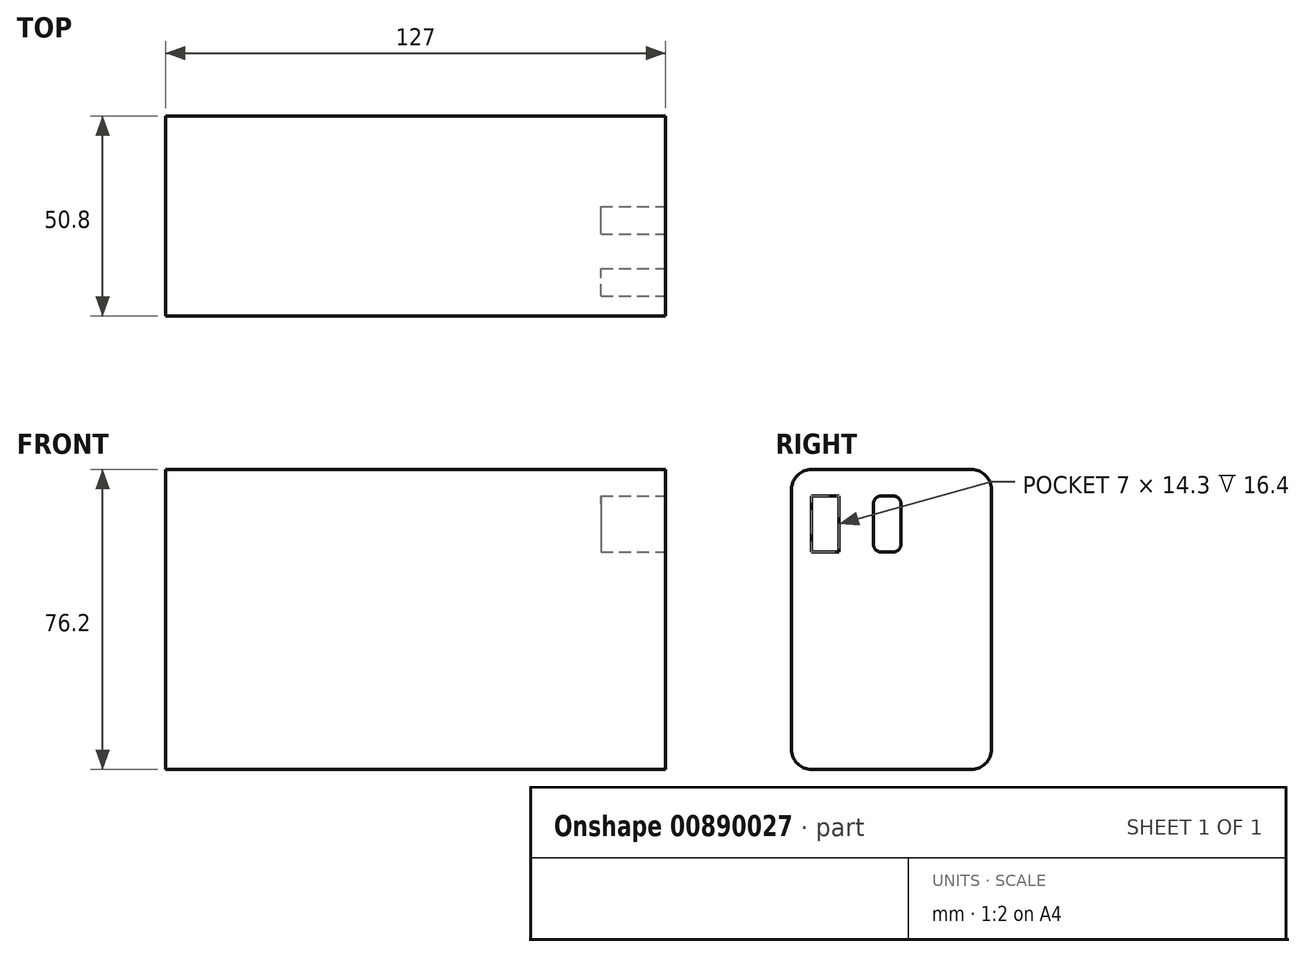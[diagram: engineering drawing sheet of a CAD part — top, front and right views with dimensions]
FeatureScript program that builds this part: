
annotation { "Feature Type Name" : "Feature", "Feature Type Description" : "" }
export const myFeature = defineFeature(function(context is Context, id is Id, definition is map)
    precondition{}
    {
        {
            var Q0;
            Q0=qCreatedBy(makeId("Front.planeOp"),FACE);
            var sketch = newSketch(context, id + "F0", { "sketchPlane" : qUnion([Q0])});
            skLineSegment(sketch, "E0.bottom", {"start": v(63.5, -38.1) * mm, "end": v(-63.5, -38.1) * mm});
            skLineSegment(sketch, "E0.top", {"start": v(63.5, 38.1) * mm, "end": v(-63.5, 38.1) * mm});
            skLineSegment(sketch, "E0.left", {"start": v(63.5, -38.1) * mm, "end": v(63.5, 38.1) * mm});
            skLineSegment(sketch, "E0.right", {"start": v(-63.5, -38.1) * mm, "end": v(-63.5, 38.1) * mm});
            skPoint(sketch, "E0.middle", {"position": v(0, 0) * mm});
            skSolve(sketch);
        }
        {
            var Q0;
            Q0=makeQuery(id+"F0.imprint","IMPRINT",FACE,{"disambiguationData":[TD([[makeQuery(id+"F0.imprint","IMPRINT",EDGE,{"derivedFrom":sQuery(id+"F0.wireOp",EDGE,"E0.bottom")}),-1.0]])]});
            extrude(context, id + "F1", {"entities" : qUnion([Q0]), "depth" : 50.8 * mm, "offsetDistance" : 25.4 * mm});
        }
        {
            var Q0;
            Q0=makeQuery(id+"F1.opExtrude","CAP_EDGE",EDGE,{"disambiguationData":[OSD([sQuery(id+"F0.wireOp",EDGE,"E0.top")])],"isStart":false});
            var Q1;
            Q1=makeQuery(id+"F1.opExtrude","CAP_EDGE",EDGE,{"disambiguationData":[OSD([sQuery(id+"F0.wireOp",EDGE,"E0.top")])],"isStart":true});
            var Q2;
            Q2=makeQuery(id+"F1.opExtrude","CAP_EDGE",EDGE,{"disambiguationData":[OSD([sQuery(id+"F0.wireOp",EDGE,"E0.bottom")])],"isStart":true});
            var Q3;
            Q3=makeQuery(id+"F1.opExtrude","CAP_EDGE",EDGE,{"disambiguationData":[OSD([sQuery(id+"F0.wireOp",EDGE,"E0.bottom")])],"isStart":false});
            fillet(context, id + "F2", {"entities" : qUnion([Q0, Q1, Q2, Q3]), "radius" : 5.08 * mm, "tangentPropagation" : true, "allowEdgeOverflow" : false});
        }
        {
            var Q0;
            Q0=makeQuery(id+"F1.opExtrude","SWEPT_FACE",FACE,{"disambiguationData":[OSD([sQuery(id+"F0.wireOp",EDGE,"E0.left")])]});
            var sketch = newSketch(context, id + "F3", { "sketchPlane" : qUnion([Q0])});
            skLineSegment(sketch, "E1.bottom", {"start": v(-45.72, 31.4) * mm, "end": v(-38.72, 31.4) * mm});
            skLineSegment(sketch, "E1.top", {"start": v(-45.72, 17.1) * mm, "end": v(-38.72, 17.1) * mm});
            skLineSegment(sketch, "E1.left", {"start": v(-45.72, 31.4) * mm, "end": v(-45.72, 17.1) * mm});
            skLineSegment(sketch, "E1.right", {"start": v(-38.72, 31.4) * mm, "end": v(-38.72, 17.1) * mm});
            skSolve(sketch);
        }
        {
            var Q0;
            Q0=makeQuery(id+"F3.imprint","IMPRINT",FACE,{"disambiguationData":[TD([[makeQuery(id+"F3.imprint","IMPRINT",EDGE,{"derivedFrom":sQuery(id+"F3.wireOp",EDGE,"E1.bottom")}),-1.0]])]});
            extrude(context, id + "F4", {"entities" : qUnion([Q0]), "operationType" : NewBodyOperationType.REMOVE, "oppositeDirection" : true, "depth" : 16.4 * mm, "offsetDistance" : 25.4 * mm});
        }
        {
            var Q0;
            Q0=makeQuery(id+"F1.opExtrude","SWEPT_FACE",FACE,{"disambiguationData":[OSD([sQuery(id+"F0.wireOp",EDGE,"E0.left")])]});
            var sketch = newSketch(context, id + "F5", { "sketchPlane" : qUnion([Q0])});
            skLineSegment(sketch, "E2.bottom", {"start": v(-27.99, 31.4) * mm, "end": v(-24.99, 31.4) * mm});
            skLineSegment(sketch, "E2.top", {"start": v(-27.99, 17.1) * mm, "end": v(-24.99, 17.1) * mm});
            skLineSegment(sketch, "E2.left", {"start": v(-29.99, 29.4) * mm, "end": v(-29.99, 19.1) * mm});
            skLineSegment(sketch, "E2.right", {"start": v(-22.99, 29.4) * mm, "end": v(-22.99, 19.1) * mm});
            skPoint(sketch, "E3.visualSharp", {"position": v(-29.99, 31.4) * mm});
            skArc(sketch, "E3.filletArc", {"start": v(-27.99, 31.4) * mm, "mid": v(-29.4, 30.81) * mm, "end": v(-29.99, 29.4) * mm});
            skPoint(sketch, "E4.visualSharp", {"position": v(-29.99, 17.1) * mm});
            skArc(sketch, "E4.filletArc", {"start": v(-29.99, 19.1) * mm, "mid": v(-29.4, 17.69) * mm, "end": v(-27.99, 17.1) * mm});
            skPoint(sketch, "E5.visualSharp", {"position": v(-22.99, 17.1) * mm});
            skArc(sketch, "E5.filletArc", {"start": v(-24.99, 17.1) * mm, "mid": v(-23.57, 17.69) * mm, "end": v(-22.99, 19.1) * mm});
            skPoint(sketch, "E6.visualSharp", {"position": v(-22.99, 31.4) * mm});
            skArc(sketch, "E6.filletArc", {"start": v(-22.99, 29.4) * mm, "mid": v(-23.57, 30.81) * mm, "end": v(-24.99, 31.4) * mm});
            skSolve(sketch);
        }
        {
            var Q0;
            Q0=makeQuery(id+"F5.imprint","IMPRINT",FACE,{"disambiguationData":[TD([[makeQuery(id+"F5.imprint","IMPRINT",EDGE,{"derivedFrom":sQuery(id+"F5.wireOp",EDGE,"E2.bottom")}),-1.0]])]});
            extrude(context, id + "F6", {"entities" : qUnion([Q0]), "operationType" : NewBodyOperationType.REMOVE, "oppositeDirection" : true, "depth" : 16.4 * mm, "offsetDistance" : 25.4 * mm});
        }
    });
